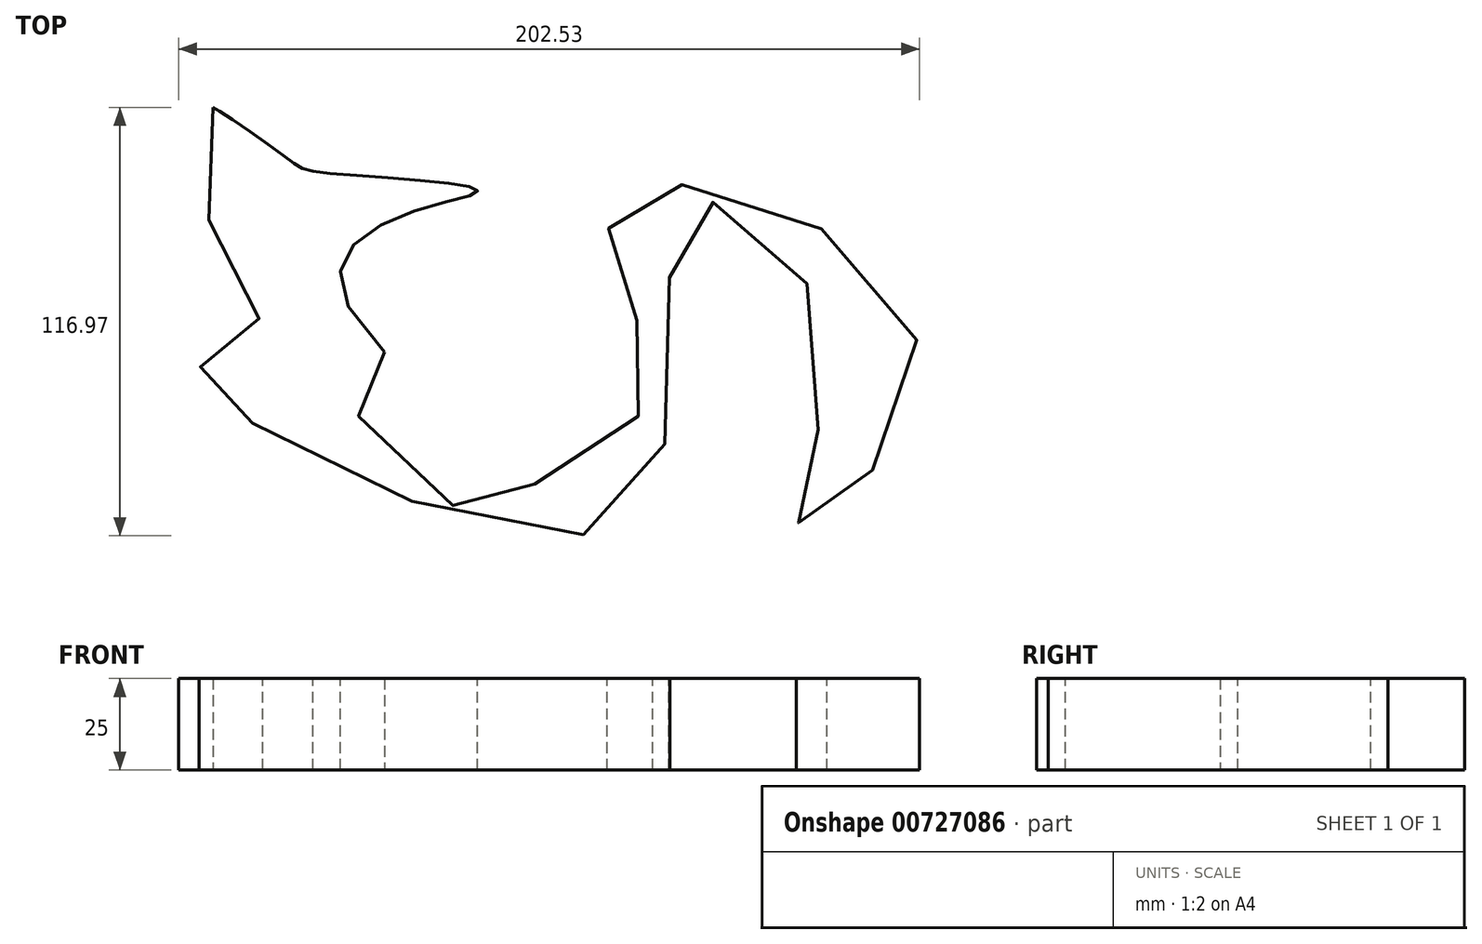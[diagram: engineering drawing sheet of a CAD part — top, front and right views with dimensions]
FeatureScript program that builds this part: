
annotation { "Feature Type Name" : "Feature", "Feature Type Description" : "" }
export const myFeature = defineFeature(function(context is Context, id is Id, definition is map)
    precondition{}
    {
        {
            var Q0;
            Q0=qCreatedBy(makeId("Top.planeOp"),FACE);
            var sketch = newSketch(context, id + "F0", { "sketchPlane" : qUnion([Q0])});
            skFitSpline(sketch, "E0", {"points": [v(-16.27, -0.06) * mm, v(-13.62, -28.2) * mm, v(11.5, -40.9) * mm, v(56.46, -11.07) * mm, v(44.54, 29.75) * mm, v(67.18, 45.71) * mm, v(129.92, -3.46) * mm, v(97.27, -46.94) * mm, v(103.71, 6.22) * mm, v(66.23, 39.2) * mm, v(53, -43.08) * mm, v(-51.69, -19.78) * mm, v(-65.89, -2.85) * mm, v(-49.63, 14.28) * mm, v(-63.2, 66.8) * mm], "startDerivative": vector(-2083.49, 889.74) * mm, "endDerivative": vector(1046.48, 564.67) * mm});
            skFitSpline(sketch, "E1", {"points": [v(-63.2, 66.8) * mm, v(-43.41, 53.35) * mm, v(-32.26, 48.9) * mm, v(8.53, 43.35) * mm, v(-16.27, -0.06) * mm], "startDerivative": vector(12.08, -0.67) * mm, "endDerivative": vector(332.68, -320.98) * mm});
            skPoint(sketch, "E2", {"position": v(-56.86, 62.85) * mm});
            skPoint(sketch, "E3", {"position": v(-61.77, 66.04) * mm});
            skSolve(sketch);
        }
        {
            var Q0;
            Q0 = qSketchRegion(id + "F0", true);
            extrude(context, id + "F1", {"entities" : qUnion([Q0]), "depth" : 25 * mm, "offsetDistance" : 25.4 * mm});
        }
        {
            var Q0;
            Q0 = qSketchRegion(id + "F0", true);
            extrude(context, id + "F2", {"entities" : qUnion([Q0]), "operationType" : NewBodyOperationType.ADD, "depth" : 25 * mm, "offsetDistance" : 25 * mm});
        }
    });
